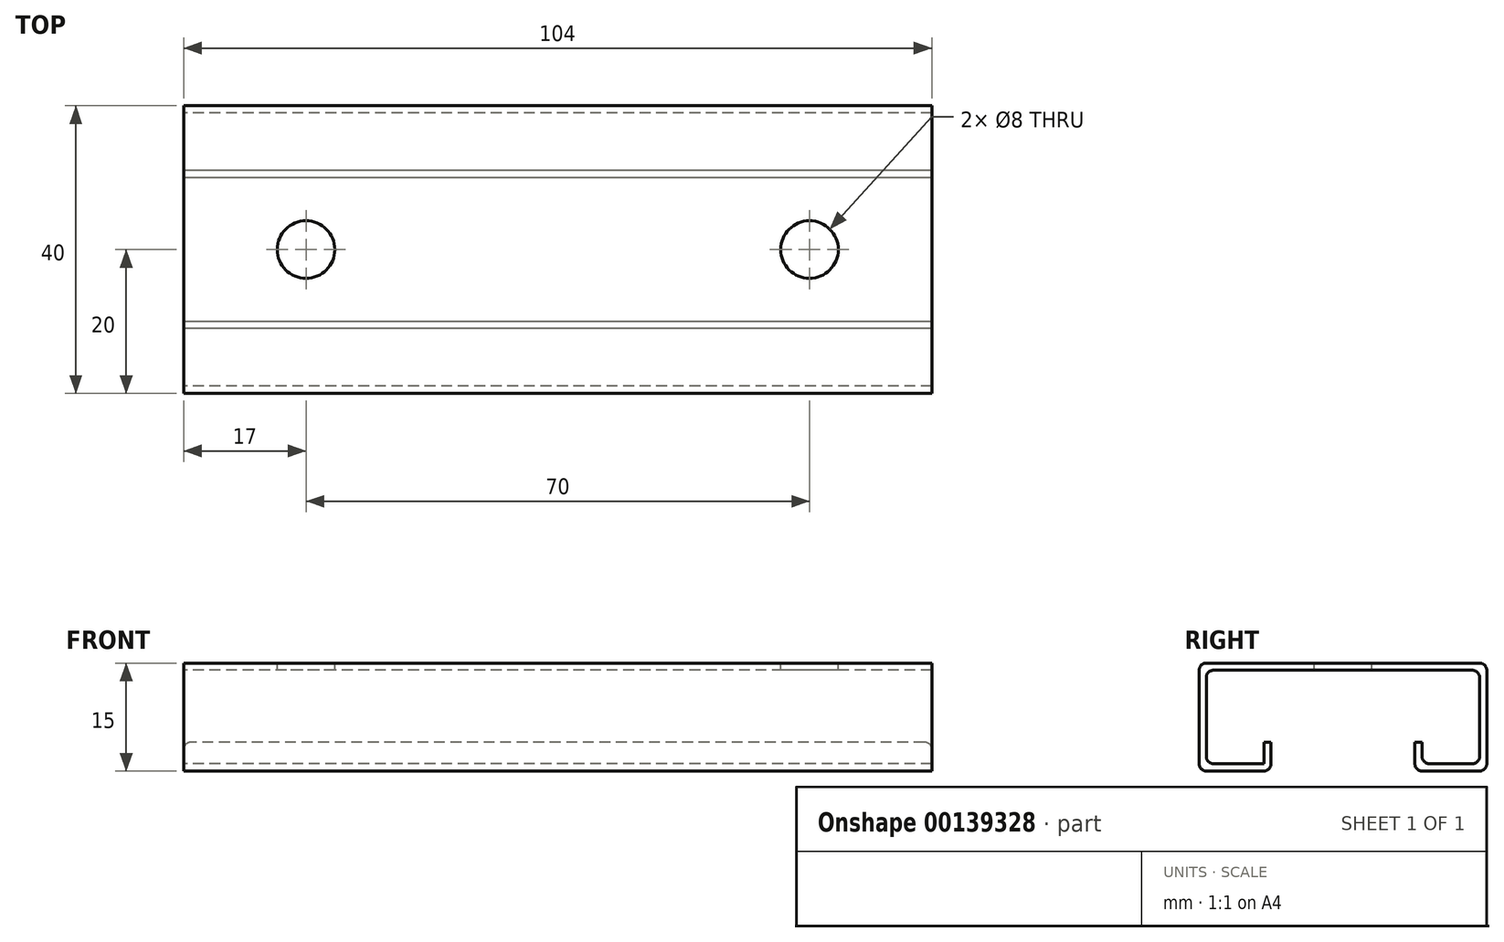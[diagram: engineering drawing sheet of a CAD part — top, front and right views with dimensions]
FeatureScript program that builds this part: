
annotation { "Feature Type Name" : "Feature", "Feature Type Description" : "" }
export const myFeature = defineFeature(function(context is Context, id is Id, definition is map)
    precondition{}
    {
        {
            var Q0;
            Q0=qCreatedBy(makeId("Right.planeOp"),FACE);
            var sketch = newSketch(context, id + "F0", { "sketchPlane" : qUnion([Q0])});
            skLineSegment(sketch, "E0", {"start": v(-20, 0) * mm, "end": v(20, 0) * mm});
            skLineSegment(sketch, "E1", {"start": v(0, -50) * mm, "end": v(0, 50) * mm, "construction": true});
            skLineSegment(sketch, "E2", {"start": v(20, 0) * mm, "end": v(20, -15) * mm});
            skLineSegment(sketch, "E3", {"start": v(20, -15) * mm, "end": v(10, -15) * mm});
            skLineSegment(sketch, "E4", {"start": v(10, -15) * mm, "end": v(10, -11) * mm});
            skLineSegment(sketch, "E5.MirrorCS", {"start": v(-10, -15) * mm, "end": v(-10, -11) * mm});
            skLineSegment(sketch, "E6.MirrorCS", {"start": v(-20, -15) * mm, "end": v(-10, -15) * mm});
            skLineSegment(sketch, "E7.MirrorCS", {"start": v(-20, 0) * mm, "end": v(-20, -15) * mm});
            skLineSegment(sketch, "E8.0", {"start": v(19, -14) * mm, "end": v(11, -14) * mm});
            skLineSegment(sketch, "E9.0", {"start": v(19, -1) * mm, "end": v(19, -14) * mm});
            skLineSegment(sketch, "E10.0", {"start": v(-19, -1) * mm, "end": v(19, -1) * mm});
            skLineSegment(sketch, "E10.1", {"start": v(-19, -1) * mm, "end": v(-19, -14) * mm});
            skLineSegment(sketch, "E11.0", {"start": v(-19, -14) * mm, "end": v(-11, -14) * mm});
            skLineSegment(sketch, "E12.0", {"start": v(-11, -14) * mm, "end": v(-11, -11) * mm});
            skLineSegment(sketch, "E13.0", {"start": v(11, -14) * mm, "end": v(11, -11) * mm});
            skLineSegment(sketch, "E14", {"start": v(-10, -11) * mm, "end": v(-11, -11) * mm});
            skLineSegment(sketch, "E15", {"start": v(10, -11) * mm, "end": v(11, -11) * mm});
            skSolve(sketch);
        }
        {
            var Q0;
            Q0=makeQuery(id+"F0.imprint","IMPRINT",FACE,{"disambiguationData":[TD([[makeQuery(id+"F0.imprint","IMPRINT",EDGE,{"derivedFrom":sQuery(id+"F0.wireOp",EDGE,"E0")}),-1.0]])]});
            var Q1;
            Q1 = qSketchRegion(id + "F0", true);
            extrude(context, id + "F1", {"entities" : qUnion([Q0, Q1]), "endBound" : BoundingType.SYMMETRIC, "depth" : 104 * mm});
        }
        {
            var Q0;
            Q0=qCreatedBy(makeId("Top.planeOp"),FACE);
            var sketch = newSketch(context, id + "F2", { "sketchPlane" : qUnion([Q0])});
            skLineSegment(sketch, "E16", {"start": v(-51.1, 0) * mm, "end": v(51.95, 0) * mm, "construction": true});
            skCircle(sketch, "E17", {"center": v(-35, 0) * mm, "radius": 4 * mm});
            skLineSegment(sketch, "E18", {"start": v(0, -30.1) * mm, "end": v(0, 37.4) * mm, "construction": true});
            skCircle(sketch, "E19.MirrorC", {"center": v(35, 0) * mm, "radius": 4 * mm});
            skSolve(sketch);
        }
        {
            var Q0;
            Q0 = qSketchRegion(id + "F2", true);
            extrude(context, id + "F3", {"entities" : qUnion([Q0]), "operationType" : NewBodyOperationType.REMOVE, "endBound" : BoundingType.SYMMETRIC, "oppositeDirection" : true, "depth" : 25 * mm});
        }
        {
            var Q0;
            Q0=makeQuery(id+"F1.opExtrude","SWEPT_EDGE",EDGE,{"disambiguationData":[OSD([sQuery(id+"F0.wireOp",EDGE,"E6.MirrorCS"),sQuery(id+"F0.wireOp",EDGE,"E7.MirrorCS")])]});
            var Q1;
            Q1=makeQuery(id+"F1.opExtrude","SWEPT_EDGE",EDGE,{"disambiguationData":[OSD([sQuery(id+"F0.wireOp",EDGE,"E0"),sQuery(id+"F0.wireOp",EDGE,"E7.MirrorCS")])]});
            var Q2;
            Q2=makeQuery(id+"F1.opExtrude","SWEPT_EDGE",EDGE,{"disambiguationData":[OSD([sQuery(id+"F0.wireOp",EDGE,"E5.MirrorCS"),sQuery(id+"F0.wireOp",EDGE,"E6.MirrorCS")])]});
            var Q3;
            Q3=makeQuery(id+"F1.opExtrude","SWEPT_EDGE",EDGE,{"disambiguationData":[OSD([sQuery(id+"F0.wireOp",EDGE,"E3"),sQuery(id+"F0.wireOp",EDGE,"E4")])]});
            var Q4;
            Q4=makeQuery(id+"F1.opExtrude","SWEPT_EDGE",EDGE,{"disambiguationData":[OSD([sQuery(id+"F0.wireOp",EDGE,"E2"),sQuery(id+"F0.wireOp",EDGE,"E3")])]});
            var Q5;
            Q5=makeQuery(id+"F1.opExtrude","SWEPT_EDGE",EDGE,{"disambiguationData":[OSD([sQuery(id+"F0.wireOp",EDGE,"E0"),sQuery(id+"F0.wireOp",EDGE,"E2")])]});
            var Q6;
            Q6=makeQuery(id+"F1.opExtrude","SWEPT_EDGE",EDGE,{"disambiguationData":[OSD([sQuery(id+"F0.wireOp",EDGE,"E8.0"),sQuery(id+"F0.wireOp",EDGE,"E9.0")])]});
            var Q7;
            Q7=makeQuery(id+"F1.opExtrude","SWEPT_EDGE",EDGE,{"disambiguationData":[OSD([sQuery(id+"F0.wireOp",EDGE,"E10.1"),sQuery(id+"F0.wireOp",EDGE,"E11.0")])]});
            fillet(context, id + "F4", {"entities" : qUnion([Q0, Q1, Q2, Q3, Q4, Q5, Q6, Q7]), "radius" : 1 * mm, "tangentPropagation" : true, "allowEdgeOverflow" : false});
        }
        {
            var Q0;
            Q0=makeQuery(id+"F1.opExtrude","SWEPT_EDGE",EDGE,{"disambiguationData":[OSD([sQuery(id+"F0.wireOp",EDGE,"E8.0"),sQuery(id+"F0.wireOp",EDGE,"E13.0")])]});
            var Q1;
            Q1=makeQuery(id+"F1.opExtrude","SWEPT_EDGE",EDGE,{"disambiguationData":[OSD([sQuery(id+"F0.wireOp",EDGE,"E9.0"),sQuery(id+"F0.wireOp",EDGE,"E10.0")])]});
            var Q2;
            Q2=makeQuery(id+"F1.opExtrude","SWEPT_EDGE",EDGE,{"disambiguationData":[OSD([sQuery(id+"F0.wireOp",EDGE,"E10.0"),sQuery(id+"F0.wireOp",EDGE,"E10.1")])]});
            fillet(context, id + "F5", {"entities" : qUnion([Q0, Q1, Q2]), "radius" : 1 * mm, "tangentPropagation" : true, "allowEdgeOverflow" : false});
        }
        {
            var Q0;
            Q0=makeQuery(id+"F1.opExtrude","CAP_EDGE",EDGE,{"disambiguationData":[OSD([sQuery(id+"F0.wireOp",EDGE,"E14")])],"isStart":false});
            var Q1;
            Q1=makeQuery(id+"F1.opExtrude","CAP_EDGE",EDGE,{"disambiguationData":[OSD([sQuery(id+"F0.wireOp",EDGE,"E15")])],"isStart":false});
            var Q2;
            Q2=makeQuery(id+"F1.opExtrude","CAP_EDGE",EDGE,{"disambiguationData":[OSD([sQuery(id+"F0.wireOp",EDGE,"E15")])],"isStart":true});
            var Q3;
            Q3=makeQuery(id+"F1.opExtrude","CAP_EDGE",EDGE,{"disambiguationData":[OSD([sQuery(id+"F0.wireOp",EDGE,"E14")])],"isStart":true});
            fillet(context, id + "F6", {"entities" : qUnion([Q0, Q1, Q2, Q3]), "radius" : 1 * mm, "tangentPropagation" : true, "allowEdgeOverflow" : false});
        }
    });
